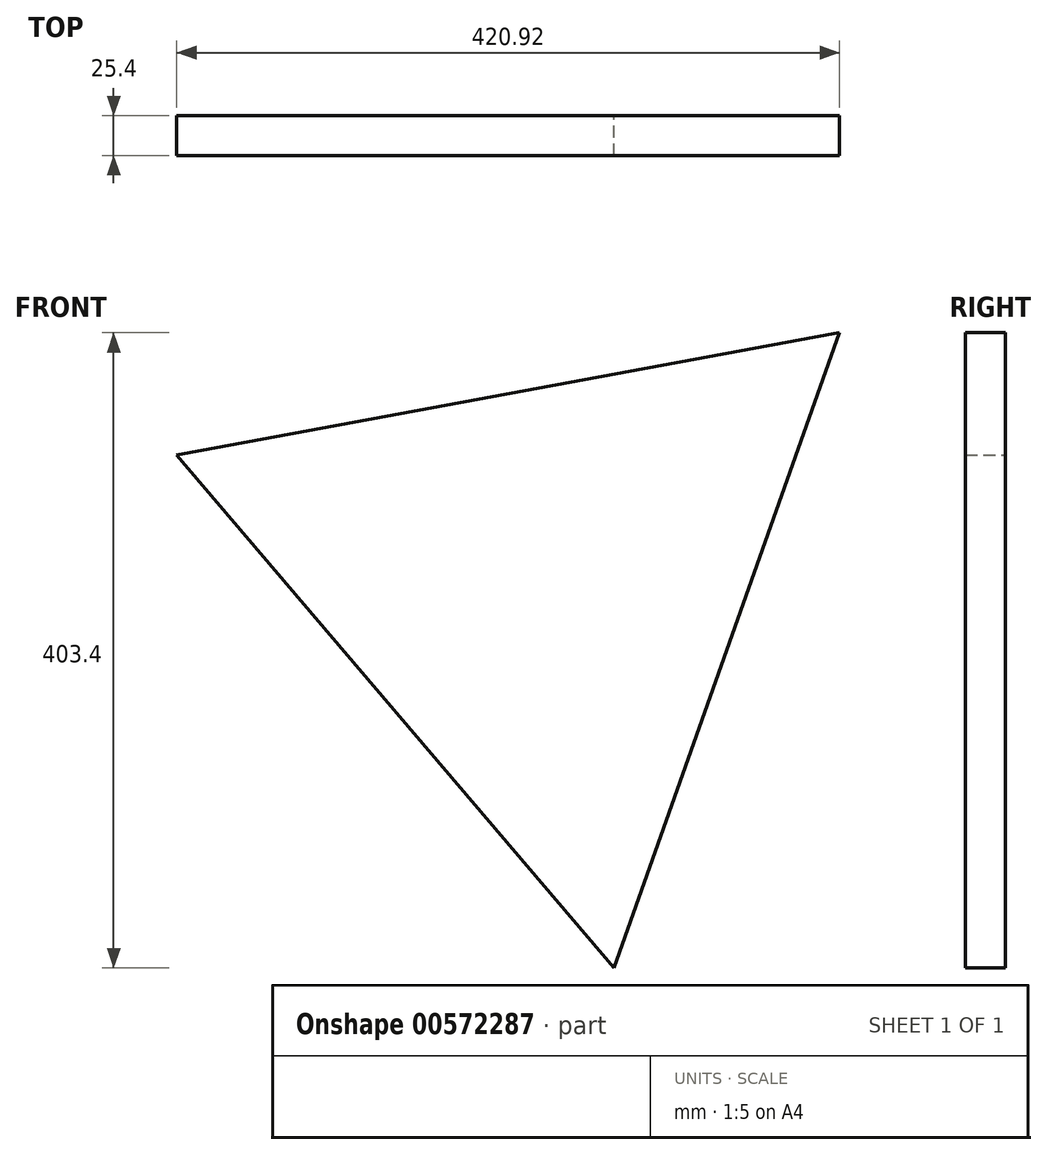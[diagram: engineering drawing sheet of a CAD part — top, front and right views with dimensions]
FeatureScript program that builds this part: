
annotation { "Feature Type Name" : "Feature", "Feature Type Description" : "" }
export const myFeature = defineFeature(function(context is Context, id is Id, definition is map)
    precondition{}
    {
        {
            var Q0;
            Q0=qCreatedBy(makeId("Front.planeOp"),FACE);
            var sketch = newSketch(context, id + "F0", { "sketchPlane" : qUnion([Q0])});
            skCircle(sketch, "E0.cCircle", {"center": v(0, 0) * mm, "radius": 123.56 * mm, "construction": true});
            skLineSegment(sketch, "E0.0", {"start": v(-232.9, 82.64) * mm, "end": v(188.02, 160.38) * mm});
            skLineSegment(sketch, "E0.1", {"start": v(188.02, 160.38) * mm, "end": v(44.88, -243.02) * mm});
            skLineSegment(sketch, "E0.2", {"start": v(44.88, -243.02) * mm, "end": v(-232.9, 82.64) * mm});
            skPoint(sketch, "E0.0.midPoint", {"position": v(-22.44, 121.5) * mm});
            skCircle(sketch, "E1.cCircle", {"center": v(394.89, 268.1) * mm, "radius": 125.22 * mm, "construction": true});
            skLineSegment(sketch, "E1.0", {"start": v(226.95, 453.89) * mm, "end": v(639.74, 320.65) * mm});
            skLineSegment(sketch, "E1.1", {"start": v(639.74, 320.65) * mm, "end": v(317.96, 29.78) * mm});
            skLineSegment(sketch, "E1.2", {"start": v(317.96, 29.78) * mm, "end": v(226.95, 453.89) * mm});
            skPoint(sketch, "E1.0.midPoint", {"position": v(433.35, 387.27) * mm});
            skSolve(sketch);
        }
        {
            var Q0;
            Q0=makeQuery(id+"F0.imprint","IMPRINT",FACE,{"disambiguationData":[TD([[makeQuery(id+"F0.imprint","IMPRINT",EDGE,{"derivedFrom":sQuery(id+"F0.wireOp",EDGE,"E0.0")}),-1.0]])]});
            extrude(context, id + "F1", {"entities" : qUnion([Q0]), "depth" : 25.4 * mm, "offsetDistance" : 25.4 * mm});
        }
    });
